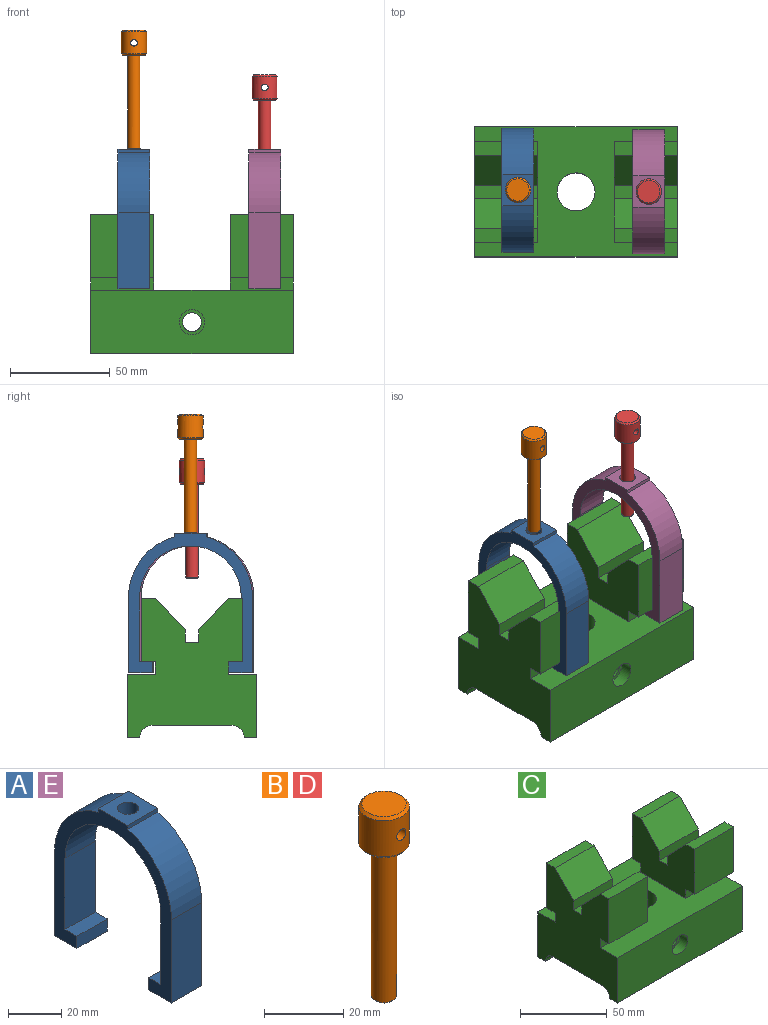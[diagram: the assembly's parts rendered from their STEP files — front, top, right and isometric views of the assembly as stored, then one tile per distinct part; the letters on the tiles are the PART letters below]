
ASSEMBLY  parts=5 mates=8
PART A: 19 faces, bbox 16x62x69.9 mm
  f0: cylinder r=25.4mm len=50.8mm, axis (-1,0,0), area 1227.2mm2, adj f13,f14,f16,f17,f18
  f1: plane 16x5.59mm, normal (0,-1,0), area 89.4mm2, adj f2,f15,f16,f17
  f2: plane 16x11.94mm, normal (0,0,-1), area 191mm2, adj f1,f3,f16,f17
  f3: plane 38.1x16mm, normal (0,1,0), area 609.7mm2, adj f2,f4,f16,f17
  f4: cylinder r=30.99mm len=29.97mm, axis (-1,0,0), area 651.5mm2, adj f3,f5,f16,f17
  f5: plane 16x1.78mm, normal (0,1,0), area 28.5mm2, adj f4,f6,f16,f17
  f6: plane 16x15.75mm, normal (0,0,1), area 202.4mm2, adj f5,f7,f16,f17,f18
  f7: plane 16x1.78mm, normal (0,-1,0), area 28.5mm2, adj f6,f8,f16,f17
  f8: cylinder r=30.99mm len=29.97mm, axis (-1,0,0), area 651.5mm2, adj f7,f9,f16,f17
  f9: plane 38.1x16mm, normal (0,-1,0), area 609.7mm2, adj f8,f10,f16,f17
  f10: plane 16x11.94mm, normal (0,0,-1), area 191mm2, adj f9,f11,f16,f17
  f11: plane 16x5.59mm, normal (0,1,0), area 89.4mm2, adj f10,f12,f16,f17
  f12: plane 16x6.35mm, normal (0,0,1), area 101.6mm2, adj f11,f13,f16,f17
  f13: plane 32.51x16mm, normal (0,1,0), area 520.3mm2, adj f0,f12,f16,f17
  f14: plane 32.51x16mm, normal (0,-1,0), area 520.3mm2, adj f0,f15,f16,f17
  f15: plane 16x6.35mm, normal (0,0,1), area 101.6mm2, adj f1,f14,f16,f17
  f16: plane 69.85x61.98mm, normal (1,0,0), area 1009mm2, adj f0,f1,f2,f3,f4,f5,f6,f7
  f17: plane 69.85x61.98mm, normal (-1,0,0), area 1009mm2, adj f0,f1,f2,f3,f4,f5,f6,f7
  f18: cylinder r=3.98mm len=7.95mm, axis (0,0,1), area 162.5mm2, adj f0,f6
PART B: 9 faces, bbox 12.7x12.7x59.7 mm
  f0: plane 11.18x11.18mm, normal (0,0,1), area 98.1mm2, adj f6
  f1: plane 5.33x5.33mm, normal (0,0,-1), area 22.3mm2, adj f8
  f2: cylinder r=3.17mm len=46.48mm, axis (0,0,-1), area 927.3mm2, adj f3,f8
  f3: plane 11.18x11.18mm, normal (0,0,-1), area 66.4mm2, adj f2,f5
  f4: cylinder r=6.35mm len=12.7mm, axis (0,0,-1), area 428.6mm2, adj f5,f6,f7
  f5: cone r=5.59mm half-angle=45deg, axis (0,0,1), area 40.4mm2, adj f3,f4
  f6: cone r=6.35mm half-angle=45deg, axis (0,0,-1), area 40.4mm2, adj f0,f4
  f7: cylinder r=1.65mm len=12.7mm, axis (0,-1,0), area 129.5mm2, adj f4
  f8: cone r=2.67mm half-angle=45deg, axis (0,0,1), area 13.2mm2, adj f1,f2
PART C: 45 faces, bbox 101.6x65x69.9 mm
  f0: cylinder r=4.76mm len=24.26mm, axis (0,-1,0), area 706.6mm2, adj f17,f44
  f1: plane 31.75x31.75mm, normal (0,-1,0), area 1008.1mm2, adj f7,f8,f13,f37
  f2: plane 31.75x31.75mm, normal (0,1,0), area 1008.1mm2, adj f7,f8,f10,f39
  f3: plane 31.75x31.75mm, normal (0,1,0), area 1008.1mm2, adj f5,f6,f9,f42
  f4: plane 31.75x31.75mm, normal (0,-1,0), area 1008.1mm2, adj f5,f6,f12,f40
  f5: plane 69.85x65.02mm, normal (1,0,0), area 3141.5mm2, adj f3,f4,f9,f11,f12,f14,f15,f16
  f6: plane 50.8x38.1mm, normal (-1,0,0), area 1463.2mm2, adj f3,f4,f9,f12,f15,f29,f30,f31
  f7: plane 69.85x65.02mm, normal (-1,0,0), area 3212.8mm2, adj f1,f2,f10,f11,f13,f14,f15,f16
  f8: plane 50.8x38.1mm, normal (1,0,0), area 1463.2mm2, adj f1,f2,f10,f13,f15,f26,f27,f28
  f9: plane 31.75x7.11mm, normal (0,0,1), area 225.8mm2, adj f3,f5,f6,f35
  f10: plane 31.75x7.11mm, normal (0,0,1), area 225.8mm2, adj f2,f7,f8,f33
  f11: plane 101.6x6.35mm, normal (0,0,-1), area 645.2mm2, adj f5,f7,f17,f21
  f12: plane 31.75x7.11mm, normal (0,0,1), area 225.8mm2, adj f4,f5,f6,f34
  f13: plane 31.75x7.11mm, normal (0,0,1), area 225.8mm2, adj f1,f7,f8,f32
  f14: plane 101.6x6.35mm, normal (0,0,-1), area 645.2mm2, adj f5,f7,f16,f23
  f15: plane 101.6x65.02mm, normal (0,0,1), area 3998.8mm2, adj f5,f6,f7,f8,f16,f17,f36,f38
  f16: plane 101.6x31.75mm, normal (0,-1,0), area 3099.1mm2, adj f5,f7,f14,f15,f20
  f17: plane 101.6x31.75mm, normal (0,1,0), area 3154.5mm2, adj f0,f5,f7,f11,f15
  f18: cylinder r=4.76mm len=17.91mm, axis (0,-1,0), area 516.6mm2, adj f19,f44
  f19: plane 12.7x12.7mm, normal (0,-1,0), area 55.4mm2, adj f18,f20
  f20: cylinder r=6.35mm len=12.7mm, axis (0,-1,0), area 253.4mm2, adj f16,f19
  f21: cylinder r=6.35mm len=101.6mm, axis (1,0,0), area 1013.4mm2, adj f5,f7,f11,f22
  f22: plane 101.6x39.62mm, normal (0,0,-1), area 3740.8mm2, adj f5,f7,f21,f23,f44
  f23: cylinder r=6.35mm len=101.6mm, axis (1,0,0), area 1013.4mm2, adj f5,f7,f14,f22
  f24: cylinder r=4.76mm len=15.88mm, axis (1,0,0), area 475mm2, adj f5,f25
  f25: cone r=0mm half-angle=59deg, axis (1,0,0), area 83.1mm2, adj f24
  f26: plane 31.75x6.35mm, normal (0,-1,0), area 201.6mm2, adj f7,f8,f27,f33
  f27: plane 31.75x6.6mm, normal (0,0,1), area 209.7mm2, adj f7,f8,f26,f28
  f28: plane 31.75x6.35mm, normal (0,1,0), area 201.6mm2, adj f7,f8,f27,f32
  f29: plane 31.75x6.35mm, normal (0,1,0), area 201.6mm2, adj f5,f6,f30,f34
  f30: plane 31.75x6.6mm, normal (0,0,1), area 209.7mm2, adj f5,f6,f29,f31
  f31: plane 31.75x6.35mm, normal (0,-1,0), area 201.6mm2, adj f5,f6,f30,f35
  f32: plane 31.75x15.75mm, normal (0,0.72,0.69), area 690.2mm2, adj f7,f8,f13,f28
  f33: plane 31.75x15.75mm, normal (0,-0.72,0.69), area 690.2mm2, adj f7,f8,f10,f26
  f34: plane 31.75x15.75mm, normal (0,0.72,0.69), area 690.2mm2, adj f5,f6,f12,f29
  f35: plane 31.75x15.75mm, normal (0,-0.72,0.69), area 690.2mm2, adj f5,f6,f9,f31
  f36: plane 31.75x6.35mm, normal (0,-1,0), area 201.6mm2, adj f7,f8,f15,f37
  f37: plane 31.75x7.11mm, normal (0,0,-1), area 225.8mm2, adj f1,f7,f8,f36
  f38: plane 31.75x6.35mm, normal (0,1,0), area 201.6mm2, adj f7,f8,f15,f39
  f39: plane 31.75x7.11mm, normal (0,0,-1), area 225.8mm2, adj f2,f7,f8,f38
  f40: plane 31.75x7.11mm, normal (0,0,-1), area 225.8mm2, adj f4,f5,f6,f41
  f41: plane 31.75x6.35mm, normal (0,-1,0), area 201.6mm2, adj f5,f6,f15,f40
  f42: plane 31.75x7.11mm, normal (0,0,-1), area 225.8mm2, adj f3,f5,f6,f43
  f43: plane 31.75x6.35mm, normal (0,1,0), area 201.6mm2, adj f5,f6,f15,f42
  f44: cylinder r=9.53mm len=25.4mm, axis (0,0,1), area 1372.6mm2, adj f0,f15,f18,f22
PART D: same geometry as B
PART E: same geometry as A
PLACE A t=(-79.61,-25.11,2.57)mm
PLACE B t=(-79.61,-25.11,72.42)mm
PLACE C t=(-50.57,6.64,-29.94)mm fixed
PLACE D t=(-14.12,-25.87,50.07)mm
PLACE E t=(-14.12,-25.87,2.57)mm
MATE cylindrical B.f2 <-> A.f18  axis (0,0,-1) through (-79.61,-25.11,72.93)mm
MATE slider A.f16 <-> C.f8  axis (1,0,0) through (-71.61,-44.16,8.16)mm
MATE slider B.f2 <-> A.f18  axis (0,0,-1) through (-79.61,-25.11,72.93)mm
MATE revolute B.f2 <-> A.f18  axis (0,0,-1) through (-79.61,-25.11,72.42)mm
MATE revolute D.f2 <-> E.f18  axis (0,0,-1) through (-14.12,-25.87,97.82)mm
MATE slider D.f2 <-> E.f18  axis (0,0,-1) through (-14.12,-25.87,50.58)mm
MATE slider E.f17 <-> C.f6  axis (-1,0,0) through (-22.12,-51.27,8.16)mm
MATE cylindrical D.f2 <-> E.f18  axis (0,0,-1) through (-14.12,-25.87,50.58)mm
